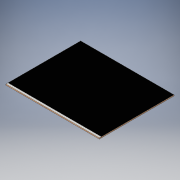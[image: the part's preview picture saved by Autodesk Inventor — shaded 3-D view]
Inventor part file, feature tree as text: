
AUTODESK INVENTOR PART (.ipt)
format: ipt  version: 2016 (Build 200138000, 138)  size: 101,376 bytes
history: native  units: in
note: dims shown in document units (in); Inventor stores cm internally (conversion verified against a paired STEP export)
features: extrude x2, sketch x2
ambient origin geometry x8: Origin, YZ Plane, XZ Plane, XY Plane, X Axis, Y Axis, Z Axis, Center Point
bodies: Solid1 (feature_tree)
feature tree (4):
  extrude  "Extrusion1"  Depth=36.0in
  extrude  "Extrusion2"  Depth=1.0in
  sketch  "Sketch1"  dims[d0=45.0in d1=36.0in]
  sketch  "Sketch2"  dims[d2=0.5in d3=0.0in d4=1.0in d5=0.001in d6=0.0in]
